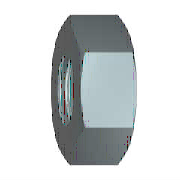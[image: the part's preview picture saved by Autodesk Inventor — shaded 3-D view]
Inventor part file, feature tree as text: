
AUTODESK INVENTOR PART (.ipt)
format: ipt  version: 2024 (Build 280153000, 153)  size: 161,280 bytes
history: native  units: mm (DEFAULTED — no unit token found)
features: chamfer x3, sketch x3, hole x1, other x1, plane x1
ambient origin geometry x7: Origin, YZ Plane, XZ Plane, X Axis, Y Axis, Z Axis, Center Point
bodies: Solid1 (feature_tree), Body (feature_tree)
feature tree (9):
  chamfer  "Chamfer1"  Angle=30.0deg  [1 undecoded]
  hole  "Thread"  [1 undecoded]
  chamfer  "Chamfer2"  Distance=4.6mm
  chamfer  "Chamfer3"  Distance=4.6mm
  other  "Work Axis1"
  plane  "Work Plane1"
  sketch  "Sketch1"  dims[d0=6.350853mm]
  sketch  "Sketch2"  dims[d1=2.4mm]
  sketch  "Sketch3"  dims[d2=0.0mm d3=30.0deg d4=30.0deg d5=4.6mm d6=4.6mm d7=90.0deg d25=2.459mm d26=6.0mm d27=4.0mm d28=2.0mm d29=14.3117mm d30=8.0mm d31=20.594885mm d8=0.270633mm d9=30.0deg d10=0.270633mm d11=30.0deg d13=0.0mm d14=0.0mm d39=0.0mm d40=0.270633mm d41=0.270633mm d42=0.0mm]
note: 2 required parameter values undecoded (feature->parameter linkage not recoverable at this tier; creation-order binding heuristic only, values carry confidence <= 0.55)
